# Revit family: DC_Holyoake_LouvreDoor_OHL_withOHL-F-45_13
name_source: partatom
category: Doors
revit_build: Autodesk Revit 2014 (Build: 20130308_1515(x64)
units: mm (PartAtom-declared; Revit-internal decimal feet)

## types (1)
- OHL-Louver Door
    Construction Type = Extruded aluminium box section to provide the strength required to hang a large louvre door
    Description = Holyoake Louvre Door System
    Door Handle Offset = 100.45 mm
    Door Hinge = Stainless Steel
    Door Jamb Depth = 101 mm  [stored 0.331365 ft]
    Door Jamb Width = 44.5 mm  [stored 0.145997 ft]
    Door Post Depth = 47 mm  [stored 0.154199 ft]
    Door Post Width = 77 mm  [stored 0.252625 ft]
    Door Transom Width = 111 mm  [stored 0.364173 ft]
    Flange Width = 25 mm  [stored 0.082021 ft]
    Frame Transom Width = 20 mm  [stored 0.0656168 ft]
    Front of Door = Rubber seal on the closing face
    Function = Interior
    Handle Z Distance = 900 mm  [stored 2.95276 ft]
    Height = 1980 mm  [stored 6.49606 ft]
    Lock = Standard Lockwood Set
    Louvre Door Panel Width = 895 mm  [stored 2.93635 ft]
    Louvre Height = 1708 mm  [stored 5.60367 ft]
    Louvre Offset = 136 mm
    Louvre Width = 735 mm  [stored 2.41142 ft]
    Manufacturer = Holyoake Industries Ltd
    Material Frame = Louver Door - Holyoake - Frame, Aluminium
    Material Handle = Louver Door - Holyoake - Handle, Stainless Steel
    Model = OHL - Louvre Door
    Opening Width = 1000 mm  [stored 3.28084 ft]
    Overall Width = 1040 mm  [stored 3.41207 ft]
    Rough Height = 1980 mm  [stored 6.49606 ft]
    Rough Width = 990 mm  [stored 3.24803 ft]
    Structural Tolerance = 5 mm  [stored 0.0164042 ft]
    Technical Data = http://www.productspec.net
    Thickness = 47 mm  [stored 0.154199 ft]
    Tolerance = 3 mm  [stored 0.00984252 ft]
    Type Comments = Louvre Door System
    URL = http://www.productspec.net
    Wall Closure = By host
    Width = 990 mm  [stored 3.24803 ft]

note: [stored X ft] marks values corroborated as IEEE doubles in the binary element streams (Revit-internal decimal feet)

## geometry (parser evidence)
native form markers: Blend x12, Sweep x13
no freeform markers — native parametric forms only
